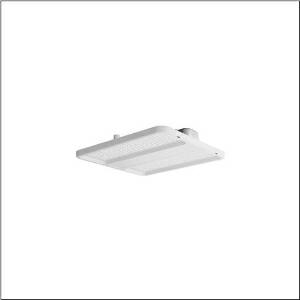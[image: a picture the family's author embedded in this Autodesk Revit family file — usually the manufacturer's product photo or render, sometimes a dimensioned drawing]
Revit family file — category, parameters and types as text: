
# Revit family: highbay_11_midi_51hn11da4mda
name_source: partatom
category: Lighting Fixtures
units: mm (PartAtom-declared; Revit-internal decimal feet)

## family parameters
Cut with Voids When Loaded = No
Host = Face
Light Source = No
Part Type = Normal
Room Calculation Point = No
Round Connector Dimension = Use Diameter
Shared = No

## types (1)
- --- (1 x LED, 4530 lm, 22.2 W, 4000K)
    Apparent Load = 22 VA
    CIE Flux Codes = 85 97 100 100 100
    Color Rendering = 80
    Color Temperature = 4000K
    Default Elevation = 1800 mm
    Description = high bay luminaire Highbay 11 midi; direct symmetric narrow distribution, light control with lens of PMMA; UGR ≤ 22 (X = 4H | Y = 8H | S = 0.25H | reflection values 70/50/20); luminous flux: 28.000lm; light colour: 840, colour temperature: 4000K, MacAdam ≤ 2 SDCM (initial), colour rendering: CRI > 80; luminous efficacy: 191lm/W; rated service life: 100.000h (L95/B50) at AT= 25°C; control: DALI 2; housing frame of high-performance plastic PA6, matt traffic white (RAL 9016); cover of PMMA; dimension (LxWxH): 474 x 442 x 72mm; luminaire connection: terminal, 5-pole, max. 2.5mm² (cable entry for one cable, Ø 8.5..16mm); mains connection: 230..240V, AC/DC 0/50..60Hz; connected load: 146,6W; protection rating (complete): IP66; insulation class (complete): insulation class I (protective earthing); protection symbol: D; impact resistance: IK08; halogen-free wiring; for central battery installations according to DIN EN 60598-2-22; corresponds to IFS (International Featured Standards) requirements for safety and quality in the food industry; LABS conformity tested according to VDMA 24364:2018-05; certification: CE, ENEC, VDE, UKCA; permissible operating ambient temperature: -40..+50°C (reducing of maximum allowable ambient temperature of 5°C with ceiling mounting); packaging unit: 1 piece; (delivery without accessories; please order mounting accessories separately)
    Height = 72 mm  [stored 0.23622 ft]
    Lamp = 1 x LED
    Lamp Light Flux = 4530 lm
    Lamp Power = 22.2 W
    Lamp count = 1
    Length = 474 mm
    Luminous efficacy = 204 lm/W
    Manufacturer = Siteco
    ModVariant = No
    Model = 51HN11DA4MDA
    Mounting Place = Ceiling
    Mounting Type = Pendant
    Number of Poles = 1
    OnlyDefault = Yes
    Power Factor = 1
    Product Name = Highbay 11 midi
    Product group = high bay luminaire
    ProductGroupID = 901
    Protection Class = Protection class I
    Protection Degree = IP 66
    RLX_Detail_Level = 1
    RLX_Emergency_Light_Flux = 0 lm
    RLX_Emergency_Type = 0
    RLX_Emergency_Type_DB = No
    RlxData = <blob elided: 16881 chars, md5=79a4aab6>
    Socket = socket
    Standby Power = 0 W
    System Light Flux = 4530 lm
    System Power = 22 W
    Type Comments = : DC mode (central or group accumulator) initial emergency light level
    Type Image = l_1363240.jpg
    URL = http://relux.com
    VarID = @adj_003723
    Voltage = 0 V
    Weight = 0.00 kg
    Width = 442 mm

note: [stored X ft] marks values corroborated as IEEE doubles in the binary element streams (Revit-internal decimal feet)

## geometry (parser evidence)
native form markers: Blend x4, Sweep x10
no freeform markers — native parametric forms only
